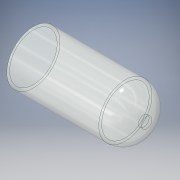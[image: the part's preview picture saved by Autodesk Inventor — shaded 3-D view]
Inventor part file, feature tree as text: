
AUTODESK INVENTOR PART (.ipt)
format: ipt  version: 2018 (Build 220112000, 112)  size: 138,240 bytes
history: native  units: in
note: dims shown in document units (in); Inventor stores cm internally (conversion verified against a paired STEP export)
features: extrude x1, fillet x1, shell x1, sketch x1
ambient origin geometry x8: Origin, YZ Plane, XZ Plane, XY Plane, X Axis, Y Axis, Z Axis, Center Point
bodies: Solid1 (feature_tree)
feature tree (4):
  extrude  "Extrusion1"  Depth=1.0in TaperAngle=0.0deg
  fillet  "Fillet1"  Radius=0.1875in
  shell  "Shell1"  Thickness=0.025in
  sketch  "Sketch1"  dims[d0=0.47in d1=1.0in d2=0.0in d3=0.1875in d4=0.025in]
